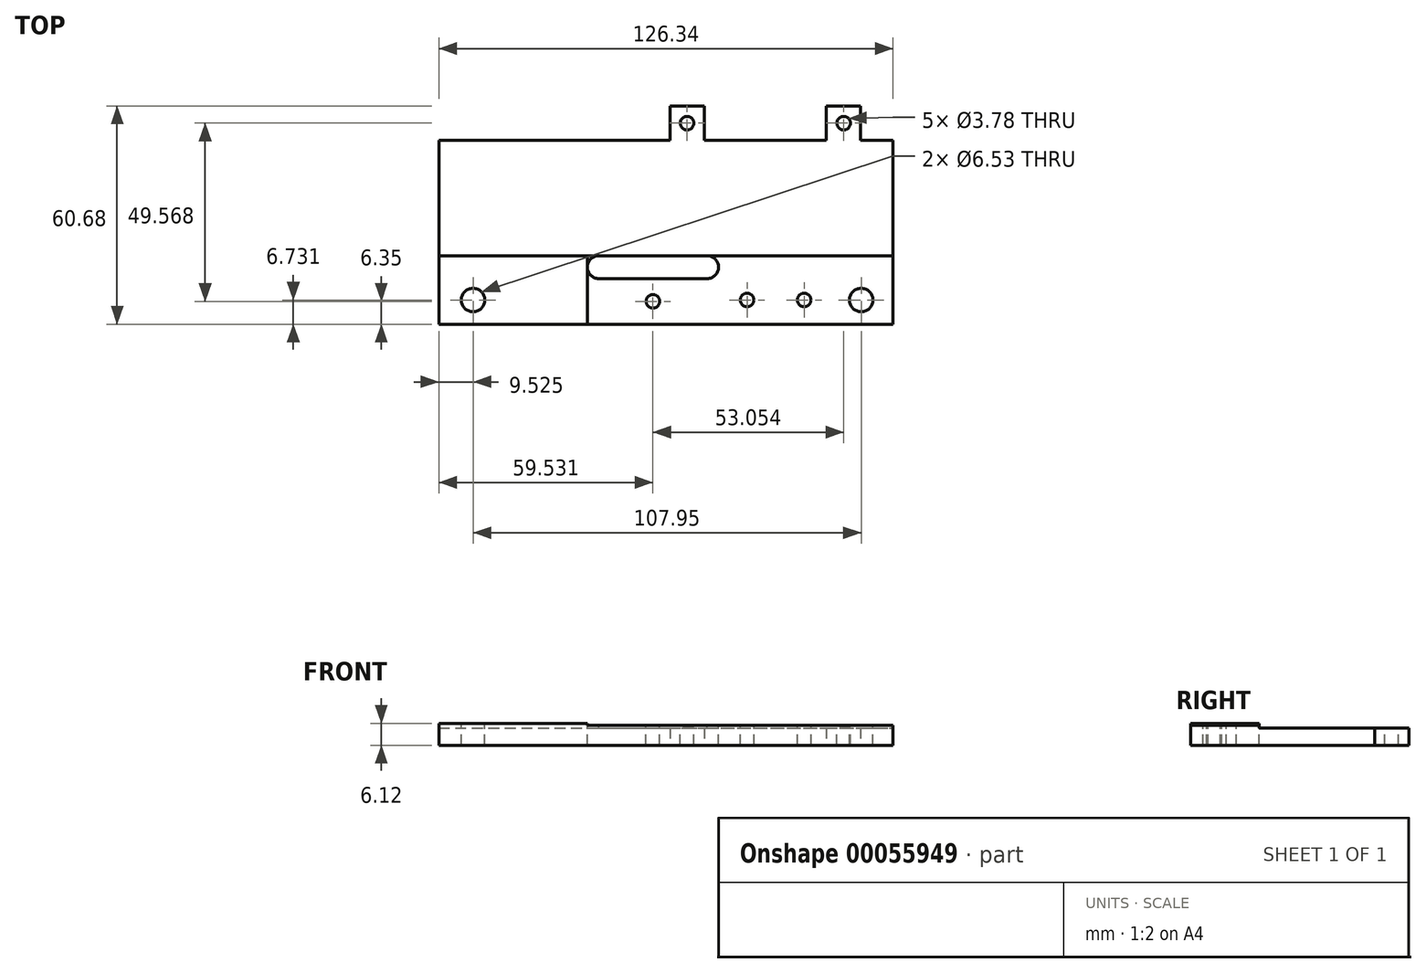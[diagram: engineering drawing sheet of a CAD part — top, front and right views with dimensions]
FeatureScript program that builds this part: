
annotation { "Feature Type Name" : "Feature", "Feature Type Description" : "" }
export const myFeature = defineFeature(function(context is Context, id is Id, definition is map)
    precondition{}
    {
        {
            var Q0;
            Q0=qCreatedBy(makeId("Top.planeOp"),FACE);
            var sketch = newSketch(context, id + "F0", { "sketchPlane" : qUnion([Q0])});
            skLineSegment(sketch, "E0", {"start": v(0, 0) * mm, "end": v(126.34, 0) * mm});
            skLineSegment(sketch, "E1", {"start": v(126.34, 0) * mm, "end": v(126.34, 51.16) * mm});
            skLineSegment(sketch, "E2", {"start": v(0, 0) * mm, "end": v(0, 51.16) * mm});
            skLineSegment(sketch, "E3", {"start": v(0, 51.16) * mm, "end": v(64.26, 51.16) * mm});
            skLineSegment(sketch, "E4", {"start": v(64.26, 51.16) * mm, "end": v(64.26, 60.68) * mm});
            skLineSegment(sketch, "E5", {"start": v(64.26, 60.68) * mm, "end": v(73.79, 60.68) * mm});
            skLineSegment(sketch, "E6", {"start": v(73.79, 60.68) * mm, "end": v(73.79, 51.16) * mm});
            skLineSegment(sketch, "E7", {"start": v(73.79, 51.16) * mm, "end": v(107.75, 51.16) * mm});
            skLineSegment(sketch, "E8", {"start": v(117.27, 51.16) * mm, "end": v(126.34, 51.16) * mm});
            skLineSegment(sketch, "E9", {"start": v(107.75, 51.16) * mm, "end": v(107.75, 60.68) * mm});
            skLineSegment(sketch, "E10", {"start": v(117.27, 51.16) * mm, "end": v(117.27, 60.68) * mm});
            skLineSegment(sketch, "E11", {"start": v(107.75, 60.68) * mm, "end": v(117.27, 60.68) * mm});
            skSolve(sketch);
        }
        {
            var Q0;
            Q0 = qSketchRegion(id + "F0", true);
            extrude(context, id + "F1", {"entities" : qUnion([Q0]), "depth" : 6.12 * mm});
        }
        {
            var Q0;
            Q0=makeQuery(id+"F1.opExtrude","CAP_FACE",FACE,{"disambiguationData":[OSD([sQuery(id+"F0.wireOp",EDGE,"E0"),sQuery(id+"F0.wireOp",EDGE,"E1"),sQuery(id+"F0.wireOp",EDGE,"E2"),sQuery(id+"F0.wireOp",EDGE,"E3"),sQuery(id+"F0.wireOp",EDGE,"E4"),sQuery(id+"F0.wireOp",EDGE,"E5"),sQuery(id+"F0.wireOp",EDGE,"E6"),sQuery(id+"F0.wireOp",EDGE,"E7"),sQuery(id+"F0.wireOp",EDGE,"b523714e-1add-4f16-8dba-c1d4d9af37d2"),sQuery(id+"F0.wireOp",EDGE,"c9321312-bc30-4a56-87c8-ecf9c79a8148"),sQuery(id+"F0.wireOp",EDGE,"3a0742eb-7e85-4fe5-9706-e3451ea161f8"),sQuery(id+"F0.wireOp",EDGE,"E8")])],"isStart":false});
            var sketch = newSketch(context, id + "F2", { "sketchPlane" : qUnion([Q0])});
            skLineSegment(sketch, "E12", {"start": v(0, 19.05) * mm, "end": v(126.34, 19.05) * mm});
            skLineSegment(sketch, "E13", {"start": v(0, 19.05) * mm, "end": v(0, 62.33) * mm});
            skLineSegment(sketch, "E14", {"start": v(0, 62.33) * mm, "end": v(126.34, 62.33) * mm});
            skLineSegment(sketch, "E15", {"start": v(126.34, 62.33) * mm, "end": v(126.34, 19.05) * mm});
            skSolve(sketch);
        }
        {
            var Q0;
            Q0 = qSketchRegion(id + "F2", true);
            extrude(context, id + "F3", {"entities" : qUnion([Q0]), "operationType" : NewBodyOperationType.REMOVE, "oppositeDirection" : true, "depth" : 1.24 * mm});
        }
        {
            var Q0;
            Q0=makeQuery(id+"F1.opExtrude","CAP_FACE",FACE,{"disambiguationData":[OSD([sQuery(id+"F0.wireOp",EDGE,"E0"),sQuery(id+"F0.wireOp",EDGE,"E1"),sQuery(id+"F0.wireOp",EDGE,"E2"),sQuery(id+"F0.wireOp",EDGE,"E3"),sQuery(id+"F0.wireOp",EDGE,"E4"),sQuery(id+"F0.wireOp",EDGE,"E5"),sQuery(id+"F0.wireOp",EDGE,"E6"),sQuery(id+"F0.wireOp",EDGE,"E7"),sQuery(id+"F0.wireOp",EDGE,"b523714e-1add-4f16-8dba-c1d4d9af37d2"),sQuery(id+"F0.wireOp",EDGE,"c9321312-bc30-4a56-87c8-ecf9c79a8148"),sQuery(id+"F0.wireOp",EDGE,"3a0742eb-7e85-4fe5-9706-e3451ea161f8"),sQuery(id+"F0.wireOp",EDGE,"E8")])],"isStart":false});
            var sketch = newSketch(context, id + "F4", { "sketchPlane" : qUnion([Q0])});
            skLineSegment(sketch, "E16", {"start": v(41.28, 0) * mm, "end": v(41.28, 19.05) * mm});
            skLineSegment(sketch, "E17", {"start": v(41.28, 19.05) * mm, "end": v(126.38, 19.05) * mm});
            skLineSegment(sketch, "E18", {"start": v(126.38, 19.05) * mm, "end": v(126.38, 0) * mm});
            skLineSegment(sketch, "E19", {"start": v(126.38, 0) * mm, "end": v(41.28, 0) * mm});
            skSolve(sketch);
        }
        {
            var Q0;
            Q0 = qSketchRegion(id + "F4", true);
            extrude(context, id + "F5", {"entities" : qUnion([Q0]), "operationType" : NewBodyOperationType.REMOVE, "oppositeDirection" : true, "depth" : 0.58 * mm});
        }
        {
            var Q0;
            Q0=makeQuery(id+"F5.boolean.opBoolean","COPY",FACE,{"derivedFrom":makeQuery(id+"F5.opExtrude","CAP_FACE",FACE,{"disambiguationData":[OSD([sQuery(id+"F4.wireOp",EDGE,"E16"),sQuery(id+"F4.wireOp",EDGE,"E17"),sQuery(id+"F4.wireOp",EDGE,"E18"),sQuery(id+"F4.wireOp",EDGE,"E19")])],"isStart":false})});
            var sketch = newSketch(context, id + "F6", { "sketchPlane" : qUnion([Q0])});
            skArc(sketch, "E20", {"start": v(44.45, 19.05) * mm, "mid": v(41.28, 15.87) * mm, "end": v(44.45, 12.7) * mm});
            skArc(sketch, "E21", {"start": v(74.61, 12.7) * mm, "mid": v(77.79, 15.88) * mm, "end": v(74.61, 19.05) * mm});
            skLineSegment(sketch, "E22", {"start": v(44.45, 12.7) * mm, "end": v(74.61, 12.7) * mm});
            skLineSegment(sketch, "E23", {"start": v(44.45, 19.05) * mm, "end": v(74.61, 19.05) * mm});
            skSolve(sketch);
        }
        {
            var Q0;
            Q0 = qSketchRegion(id + "F6", true);
            extrude(context, id + "F7", {"entities" : qUnion([Q0]), "operationType" : NewBodyOperationType.REMOVE, "endBound" : BoundingType.UP_TO_NEXT, "oppositeDirection" : true, "depth" : 25.4 * mm});
        }
        {
            var Q0;
            Q0=makeQuery(id+"F3.boolean.opBoolean","COPY",FACE,{"derivedFrom":makeQuery(id+"F3.opExtrude","CAP_FACE",FACE,{"disambiguationData":[OSD([sQuery(id+"F2.wireOp",EDGE,"E12"),sQuery(id+"F2.wireOp",EDGE,"E13"),sQuery(id+"F2.wireOp",EDGE,"E14"),sQuery(id+"F2.wireOp",EDGE,"E15")])],"isStart":false})});
            var sketch = newSketch(context, id + "F8", { "sketchPlane" : qUnion([Q0])});
            skCircle(sketch, "E24", {"center": v(69.02, 55.92) * mm, "radius": 1.9 * mm});
            skCircle(sketch, "E25", {"center": v(112.59, 55.92) * mm, "radius": 1.9 * mm});
            skSolve(sketch);
        }
        {
            var Q0;
            Q0 = qSketchRegion(id + "F8", true);
            extrude(context, id + "F9", {"entities" : qUnion([Q0]), "operationType" : NewBodyOperationType.REMOVE, "endBound" : BoundingType.UP_TO_NEXT, "oppositeDirection" : true, "depth" : 25.4 * mm});
        }
        {
            var Q0;
            {var subQ0=sQuery(id+"F4.wireOp",EDGE,"E16");var subQ1=makeQuery(id+"F5.boolean.opBoolean","COPY",FACE,{"derivedFrom":makeQuery(id+"F5.opExtrude","CAP_FACE",FACE,{"disambiguationData":[OSD([subQ0,sQuery(id+"F4.wireOp",EDGE,"E17"),sQuery(id+"F4.wireOp",EDGE,"E18"),sQuery(id+"F4.wireOp",EDGE,"E19")])],"isStart":false})});Q0=makeQuery(id+"F7.boolean.opBoolean","SPLIT",FACE,{"disambiguationData":[TD([makeQuery(id+"F1.opExtrude","SWEPT_FACE",FACE,{"disambiguationData":[OSD([sQuery(id+"F0.wireOp",EDGE,"E0")])]}),makeQuery(id+"F1.opExtrude","SWEPT_FACE",FACE,{"disambiguationData":[OSD([sQuery(id+"F0.wireOp",EDGE,"E1")])]}),makeQuery(id+"F3.boolean.opBoolean","COPY",FACE,{"derivedFrom":makeQuery(id+"F3.opExtrude","SWEPT_FACE",FACE,{"disambiguationData":[OSD([sQuery(id+"F2.wireOp",EDGE,"E12")])]})}),makeQuery(id+"F5.boolean.opBoolean","COPY",FACE,{"derivedFrom":makeQuery(id+"F5.opExtrude","SWEPT_FACE",FACE,{"disambiguationData":[OSD([subQ0])]})}),subQ1,makeQuery(id+"F7.opExtrude","SWEPT_FACE",FACE,{"disambiguationData":[OSD([sQuery(id+"F6.wireOp",EDGE,"E20")])]}),makeQuery(id+"F7.opExtrude","SWEPT_FACE",FACE,{"disambiguationData":[OSD([sQuery(id+"F6.wireOp",EDGE,"E21")])]}),makeQuery(id+"F7.opExtrude","SWEPT_FACE",FACE,{"disambiguationData":[OSD([sQuery(id+"F6.wireOp",EDGE,"E22")])]})])],"derivedFrom":subQ1});}
            var sketch = newSketch(context, id + "F10", { "sketchPlane" : qUnion([Q0])});
            skCircle(sketch, "E26", {"center": v(59.53, 6.35) * mm, "radius": 1.9 * mm});
            skPoint(sketch, "E26.centerSnap0", {"position": v(59.53, 12.7) * mm});
            skSolve(sketch);
        }
        {
            var Q0;
            Q0 = qSketchRegion(id + "F10", true);
            extrude(context, id + "F11", {"entities" : qUnion([Q0]), "operationType" : NewBodyOperationType.REMOVE, "endBound" : BoundingType.UP_TO_NEXT, "oppositeDirection" : true, "depth" : 25.4 * mm});
        }
        {
            var Q0;
            Q0=makeQuery(id+"F1.opExtrude","CAP_FACE",FACE,{"disambiguationData":[OSD([sQuery(id+"F0.wireOp",EDGE,"E0"),sQuery(id+"F0.wireOp",EDGE,"E1"),sQuery(id+"F0.wireOp",EDGE,"E2"),sQuery(id+"F0.wireOp",EDGE,"E3"),sQuery(id+"F0.wireOp",EDGE,"E4"),sQuery(id+"F0.wireOp",EDGE,"E5"),sQuery(id+"F0.wireOp",EDGE,"E6"),sQuery(id+"F0.wireOp",EDGE,"E7"),sQuery(id+"F0.wireOp",EDGE,"b523714e-1add-4f16-8dba-c1d4d9af37d2"),sQuery(id+"F0.wireOp",EDGE,"c9321312-bc30-4a56-87c8-ecf9c79a8148"),sQuery(id+"F0.wireOp",EDGE,"3a0742eb-7e85-4fe5-9706-e3451ea161f8"),sQuery(id+"F0.wireOp",EDGE,"E8")])],"isStart":false});
            var sketch = newSketch(context, id + "F12", { "sketchPlane" : qUnion([Q0])});
            skCircle(sketch, "E27", {"center": v(9.53, 6.73) * mm, "radius": 3.26 * mm});
            skSolve(sketch);
        }
        {
            var Q0;
            Q0 = qSketchRegion(id + "F12", true);
            extrude(context, id + "F13", {"entities" : qUnion([Q0]), "operationType" : NewBodyOperationType.REMOVE, "endBound" : BoundingType.UP_TO_NEXT, "oppositeDirection" : true, "depth" : 25.4 * mm});
        }
        {
            var Q0;
            {var subQ0=sQuery(id+"F4.wireOp",EDGE,"E16");var subQ1=makeQuery(id+"F5.boolean.opBoolean","COPY",FACE,{"derivedFrom":makeQuery(id+"F5.opExtrude","CAP_FACE",FACE,{"disambiguationData":[OSD([subQ0,sQuery(id+"F4.wireOp",EDGE,"E17"),sQuery(id+"F4.wireOp",EDGE,"E18"),sQuery(id+"F4.wireOp",EDGE,"E19")])],"isStart":false})});Q0=makeQuery(id+"F7.boolean.opBoolean","SPLIT",FACE,{"disambiguationData":[TD([makeQuery(id+"F1.opExtrude","SWEPT_FACE",FACE,{"disambiguationData":[OSD([sQuery(id+"F0.wireOp",EDGE,"E0")])]}),makeQuery(id+"F1.opExtrude","SWEPT_FACE",FACE,{"disambiguationData":[OSD([sQuery(id+"F0.wireOp",EDGE,"E1")])]}),makeQuery(id+"F3.boolean.opBoolean","COPY",FACE,{"derivedFrom":makeQuery(id+"F3.opExtrude","SWEPT_FACE",FACE,{"disambiguationData":[OSD([sQuery(id+"F2.wireOp",EDGE,"E12")])]})}),makeQuery(id+"F5.boolean.opBoolean","COPY",FACE,{"derivedFrom":makeQuery(id+"F5.opExtrude","SWEPT_FACE",FACE,{"disambiguationData":[OSD([subQ0])]})}),subQ1,makeQuery(id+"F7.opExtrude","SWEPT_FACE",FACE,{"disambiguationData":[OSD([sQuery(id+"F6.wireOp",EDGE,"E20")])]}),makeQuery(id+"F7.opExtrude","SWEPT_FACE",FACE,{"disambiguationData":[OSD([sQuery(id+"F6.wireOp",EDGE,"E21")])]}),makeQuery(id+"F7.opExtrude","SWEPT_FACE",FACE,{"disambiguationData":[OSD([sQuery(id+"F6.wireOp",EDGE,"E22")])]})])],"derivedFrom":subQ1});}
            var sketch = newSketch(context, id + "F14", { "sketchPlane" : qUnion([Q0])});
            skCircle(sketch, "E28", {"center": v(85.73, 6.73) * mm, "radius": 1.9 * mm});
            skCircle(sketch, "E29", {"center": v(101.6, 6.73) * mm, "radius": 1.9 * mm});
            skSolve(sketch);
        }
        {
            var Q0;
            Q0 = qSketchRegion(id + "F14", true);
            extrude(context, id + "F15", {"entities" : qUnion([Q0]), "operationType" : NewBodyOperationType.REMOVE, "endBound" : BoundingType.UP_TO_NEXT, "oppositeDirection" : true, "depth" : 25.4 * mm});
        }
        {
            var Q0;
            {var subQ0=sQuery(id+"F4.wireOp",EDGE,"E16");var subQ1=makeQuery(id+"F5.boolean.opBoolean","COPY",FACE,{"derivedFrom":makeQuery(id+"F5.opExtrude","CAP_FACE",FACE,{"disambiguationData":[OSD([subQ0,sQuery(id+"F4.wireOp",EDGE,"E17"),sQuery(id+"F4.wireOp",EDGE,"E18"),sQuery(id+"F4.wireOp",EDGE,"E19")])],"isStart":false})});Q0=makeQuery(id+"F7.boolean.opBoolean","SPLIT",FACE,{"disambiguationData":[TD([makeQuery(id+"F1.opExtrude","SWEPT_FACE",FACE,{"disambiguationData":[OSD([sQuery(id+"F0.wireOp",EDGE,"E0")])]}),makeQuery(id+"F1.opExtrude","SWEPT_FACE",FACE,{"disambiguationData":[OSD([sQuery(id+"F0.wireOp",EDGE,"E1")])]}),makeQuery(id+"F3.boolean.opBoolean","COPY",FACE,{"derivedFrom":makeQuery(id+"F3.opExtrude","SWEPT_FACE",FACE,{"disambiguationData":[OSD([sQuery(id+"F2.wireOp",EDGE,"E12")])]})}),makeQuery(id+"F5.boolean.opBoolean","COPY",FACE,{"derivedFrom":makeQuery(id+"F5.opExtrude","SWEPT_FACE",FACE,{"disambiguationData":[OSD([subQ0])]})}),subQ1,makeQuery(id+"F7.opExtrude","SWEPT_FACE",FACE,{"disambiguationData":[OSD([sQuery(id+"F6.wireOp",EDGE,"E20")])]}),makeQuery(id+"F7.opExtrude","SWEPT_FACE",FACE,{"disambiguationData":[OSD([sQuery(id+"F6.wireOp",EDGE,"E21")])]}),makeQuery(id+"F7.opExtrude","SWEPT_FACE",FACE,{"disambiguationData":[OSD([sQuery(id+"F6.wireOp",EDGE,"E22")])]})])],"derivedFrom":subQ1});}
            var sketch = newSketch(context, id + "F16", { "sketchPlane" : qUnion([Q0])});
            skCircle(sketch, "E30", {"center": v(117.48, 6.73) * mm, "radius": 3.26 * mm});
            skSolve(sketch);
        }
        {
            var Q0;
            Q0 = qSketchRegion(id + "F16", true);
            extrude(context, id + "F17", {"entities" : qUnion([Q0]), "operationType" : NewBodyOperationType.REMOVE, "endBound" : BoundingType.UP_TO_NEXT, "oppositeDirection" : true, "depth" : 25.4 * mm});
        }
    });
